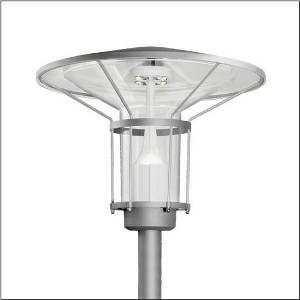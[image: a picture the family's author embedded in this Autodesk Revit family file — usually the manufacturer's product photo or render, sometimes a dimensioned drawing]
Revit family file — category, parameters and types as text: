
# Revit family: laterne_classic_iq___p1_0a_5xa5245bf14h_da05
name_source: partatom
category: Lighting Fixtures
units: mm (PartAtom-declared; Revit-internal decimal feet)

## family parameters
Cut with Voids When Loaded = No
Host = Face
Light Source = No
Part Type = Normal
Room Calculation Point = No
Round Connector Dimension = Use Diameter
Shared = No

## types (1)
- --- (1 x LED, 1360 lm, 12.9 W, 2200K)
    Apparent Load = 13 VA
    CIE Flux Codes = 30 61 91 96 100
    Color Rendering = 70
    Color Temperature = 2200K
    Default Elevation = 1800 mm
    Description = Lantern Classic iQ, mast luminaire, Module 540 iQ-SR, primary light control with 3 zone facetted reflector, of plastic, silver coated, highly specular, structured, primary optical cover: cover, of PMMA, transparent, light distribution: P1.0a, light emission: direct distribution, primary light characteristic: strongly asymmetric, installation type: post-top, LED, High Power LED, rated luminous flux: 1.360lm, luminous efficacy: 105lm/W, light colour: 722, colour temperature: 2200K, control gear: ECG iQ, control: presetting dimming logarithmic, Street-Remote, Auto-Match, Temp-Guard, Lumen-Switch, Night-Set, Smart-Wire, Light-Fading, Desk-Remote (wireless, voltage-free reading and setting of iQ features in the workshop via application-optimized NFC function/RFID function), optimised constant luminous flux control (CLO 2.0), with terminal, 6-pole, max. 2.5mm², mains connection: 220..240V, AC, 50/60Hz, start of lifetime: 13W, end of lifetime: 13W, reduction: 6W, luminaire housing, upper part, of glass-fibre reinforced polyester, coated, Siteco® metallic grey (DB 702S), diameter: 750mm, height: 596mm, spigot size: d x l = 76 x 70mm (post-top) | with reducer (optional accessory) 60 x 70mm, post-top mast mounting element, of diecast aluminium, coated, Siteco® metallic grey (DB 702S), Module 540 iQ-SR, traffic white (RAL 9016), equipment: standard, protection rating (complete): IP65, insulation class (complete): insulation class II (safety insulation), certification: CE, ENEC, VDE, packaging unit: 1 piece

Light Distribution: P1.0a
    Height = 596 mm
    Lamp = 1 x LED
    Lamp Light Flux = 1360 lm
    Lamp Power = 12.9 W
    Lamp count = 1
    Length = 750 mm
    Luminous efficacy = 105 lm/W
    Manufacturer = Siteco
    ModVariant = No
    Model = 5XA5245BF14H
    Number of Poles = 1
    OnlyDefault = Yes
    Power Factor = 1
    Product Name = Laterne Classic iQ | P1.0a
    Product group = mast luminaire | pylon top
    ProductGroupID = 6100
    Protection Class = Protection class II
    Protection Degree = IP 65
    RLX_Detail_Level = 1
    RlxData = <blob elided: 94613 chars, md5=4998dd80>
    Socket = socket
    Standby Power = 0 W
    System Light Flux = 1360 lm
    System Power = 13 W
    Type Comments = factory setting: luminous flux: 100 % | dim-lin: 254 | 516 mA
    Type Image = l_1006052.jpg
    URL = http://relux.com
    VarID = @adj_071523
    Voltage = 0 V
    Weight = 0.00 kg
    Width = 0 mm  [stored 0 ft]

note: [stored X ft] marks values corroborated as IEEE doubles in the binary element streams (Revit-internal decimal feet)

## geometry (parser evidence)
native form markers: Blend x4, Sweep x11
no freeform markers — native parametric forms only
